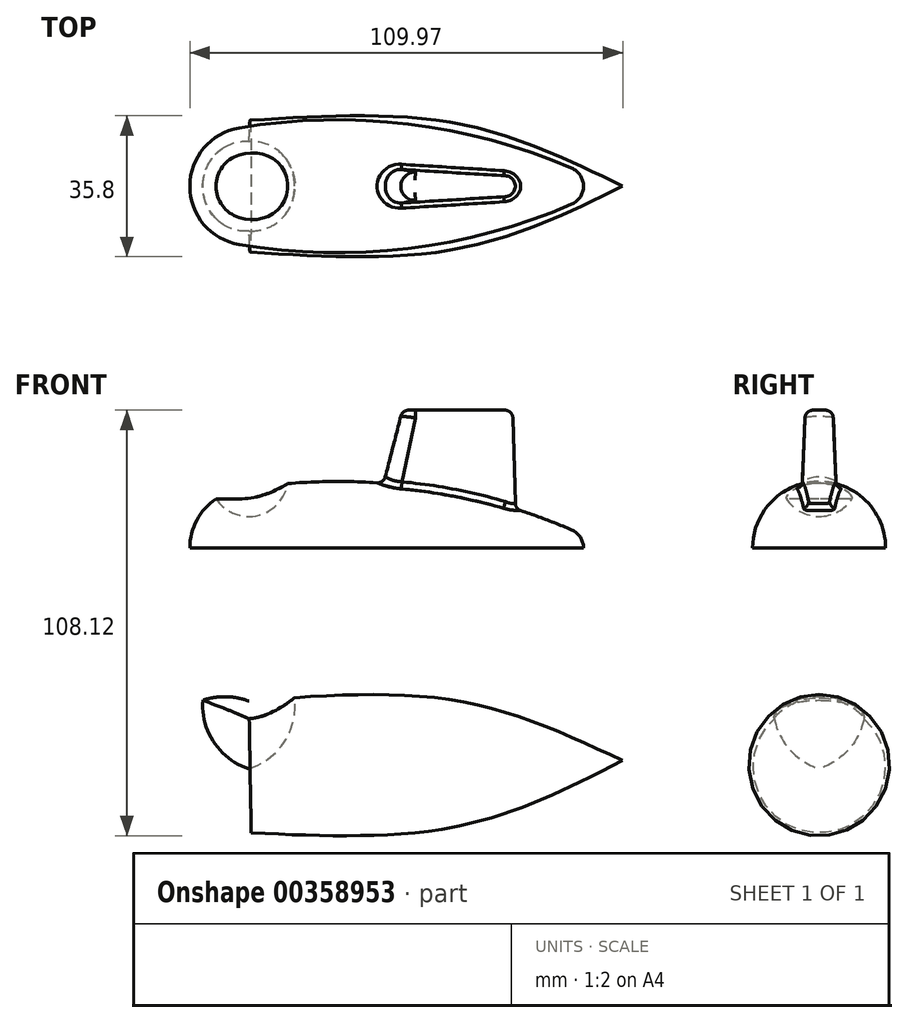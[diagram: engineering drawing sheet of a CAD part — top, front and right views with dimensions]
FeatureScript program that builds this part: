
annotation { "Feature Type Name" : "Feature", "Feature Type Description" : "" }
export const myFeature = defineFeature(function(context is Context, id is Id, definition is map)
    precondition{}
    {
        {
            var Q0;
            Q0=qCreatedBy(makeId("Top.planeOp"),FACE);
            var sketch = newSketch(context, id + "F0", { "sketchPlane" : qUnion([Q0])});
            skArc(sketch, "E0", {"start": v(-2.5, 14.8) * mm, "mid": v(-11.46, 9.68) * mm, "end": v(-15, 0) * mm});
            skArc(sketch, "E1", {"start": v(85, 0) * mm, "mid": v(84.18, 2.75) * mm, "end": v(81.98, 4.6) * mm});
            skArc(sketch, "E2", {"start": v(81.98, 4.6) * mm, "mid": v(40.48, 15.8) * mm, "end": v(-2.5, 14.8) * mm});
            skLineSegment(sketch, "E3", {"start": v(-15, 0) * mm, "end": v(85, 0) * mm});
            skSolve(sketch);
        }
        {
            var Q0;
            Q0=makeQuery(id+"F0.imprint","IMPRINT",FACE,{"disambiguationData":[TD([[makeQuery(id+"F0.imprint","IMPRINT",EDGE,{"derivedFrom":sQuery(id+"F0.wireOp",EDGE,"E0")}),1.0]])]});
            var Q1;
            Q1=sQuery(id+"F0.wireOp",EDGE,"E1");
            var Q2;
            Q2=sQuery(id+"F0.wireOp",EDGE,"E2");
            var Q3;
            Q3=sQuery(id+"F0.wireOp",EDGE,"E0");
            var Q4;
            Q4=sQuery(id+"F0.wireOp",EDGE,"E3");
            revolve(context, id + "F1", {"entities" : qUnion([Q0]), "surfaceEntities" : qUnion([Q1, Q2, Q3]), "axis" : qUnion([Q4]), "revolveType" : RevolveType.ONE_DIRECTION, "angle" : 180 * degree});
        }
        {
            var Q0;
            Q0=qCreatedBy(makeId("Front.planeOp"),FACE);
            var sketch = newSketch(context, id + "F2", { "sketchPlane" : qUnion([Q0])});
            skArc(sketch, "E4", {"start": v(0, 8) * mm, "mid": v(10, 18) * mm, "end": v(0, 28) * mm});
            skLineSegment(sketch, "E5", {"start": v(0, 28) * mm, "end": v(0, 8) * mm});
            skPoint(sketch, "E6.orphan", {"position": v(0, 42.91) * mm});
            skSolve(sketch);
        }
        {
            var Q0;
            Q0 = qSketchRegion(id + "F2", true);
            var Q1;
            Q1=sQuery(id+"F2.wireOp",EDGE,"E5");
            revolve(context, id + "F3", {"operationType" : NewBodyOperationType.REMOVE, "entities" : qUnion([Q0]), "axis" : qUnion([Q1]), "revolveType" : RevolveType.FULL, "oppositeDirection" : true});
        }
        {
            var Q0;
            Q0=qCreatedBy(makeId("Top.planeOp"),FACE);
            var sketch = newSketch(context, id + "F4", { "sketchPlane" : qUnion([Q0])});
            skArc(sketch, "E7", {"start": v(65.2, -3) * mm, "mid": v(68, 0) * mm, "end": v(65.2, 3) * mm});
            skArc(sketch, "E8", {"start": v(35.33, 4.99) * mm, "mid": v(30, 0) * mm, "end": v(35.33, -4.99) * mm});
            skLineSegment(sketch, "E9", {"start": v(35.33, -4.99) * mm, "end": v(65.2, -3) * mm});
            skLineSegment(sketch, "E10.MirrorCS", {"start": v(35.33, 4.99) * mm, "end": v(65.2, 3) * mm});
            skSolve(sketch);
        }
        {
            var Q0;
            Q0=qCreatedBy(makeId("Top.planeOp"),FACE);
            cPlane(context, id + "F5", {"entities" : qUnion([Q0]), "cplaneType" : CPlaneType.OFFSET, "offset" : 35 * mm, "width" : 150 * mm, "height" : 150 * mm});
        }
        {
            var Q0;
            Q0=qCreatedBy(id+"F5.planeOp",FACE);
            var sketch = newSketch(context, id + "F6", { "sketchPlane" : qUnion([Q0])});
            skArc(sketch, "E11", {"start": v(42.73, 3.5) * mm, "mid": v(39, 0) * mm, "end": v(42.73, -3.5) * mm});
            skArc(sketch, "E12", {"start": v(65.13, -2) * mm, "mid": v(67, 0) * mm, "end": v(65.13, 2) * mm});
            skLineSegment(sketch, "E13", {"start": v(65.13, -2) * mm, "end": v(42.73, -3.5) * mm});
            skLineSegment(sketch, "E14.MirrorCS", {"start": v(65.13, 2) * mm, "end": v(42.73, 3.5) * mm});
            skSolve(sketch);
        }
        {
            var Q1;
            Q1=makeQuery(id+"F4.imprint","IMPRINT",FACE,{"disambiguationData":[TD([[makeQuery(id+"F4.imprint","IMPRINT",EDGE,{"derivedFrom":sQuery(id+"F4.wireOp",EDGE,"E7")}),1.0]])]});
            var Q2;
            Q2=makeQuery(id+"F6.imprint","IMPRINT",FACE,{"disambiguationData":[TD([[makeQuery(id+"F6.imprint","IMPRINT",EDGE,{"derivedFrom":sQuery(id+"F6.wireOp",EDGE,"E11")}),1.0]])]});
            loft(context, id + "F7", {"operationType" : NewBodyOperationType.ADD, "sheetProfilesArray" : [{ "sheetProfileEntities" : qUnion([Q1]) }, { "sheetProfileEntities" : qUnion([Q2]) }]});
        }
        {
            var Q0;
            Q0=makeQuery(id+"F7.opLoft","CAP_FACE",FACE,{"disambiguationData":[OSD([makeQuery(id+"F6.imprint","IMPRINT",FACE,{"disambiguationData":[TD([[makeQuery(id+"F6.imprint","IMPRINT",EDGE,{"derivedFrom":sQuery(id+"F6.wireOp",EDGE,"E11")}),1.0]])]})])],"isStart":true});
            fillet(context, id + "F8", {"entities" : qUnion([Q0]), "radius" : 2 * mm, "tangentPropagation" : true, "allowEdgeOverflow" : false});
        }
        {
            var Q0;
            Q0=makeQuery(id+"F7.boolean.opBoolean","INTERSECT",EDGE,{"derivedFrom":[makeQuery(id+"F1.opRevolve","SWEPT_FACE",FACE,{"disambiguationData":[OSD([sQuery(id+"F0.wireOp",EDGE,"E2")])]}),makeQuery(id+"F7.opLoft","SWEPT_FACE",FACE,{"disambiguationData":[OSD([sQuery(id+"F4.wireOp",EDGE,"E7"),sQuery(id+"F4.wireOp",EDGE,"E8"),sQuery(id+"F4.wireOp",EDGE,"E9"),sQuery(id+"F6.wireOp",EDGE,"E11"),sQuery(id+"F6.wireOp",EDGE,"E12"),sQuery(id+"F6.wireOp",EDGE,"E13")])]})]});
            fillet(context, id + "F9", {"entities" : qUnion([Q0]), "radius" : 2 * mm, "tangentPropagation" : true, "allowEdgeOverflow" : false});
        }
        {
            var Q0;
            Q0=qCreatedBy(makeId("Front.planeOp"),FACE);
            var sketch = newSketch(context, id + "F10", { "sketchPlane" : qUnion([Q0])});
            skLineSegment(sketch, "E15", {"start": v(-23.84, -56.09) * mm, "end": v(94.97, -54.03) * mm});
            skArc(sketch, "E16", {"start": v(0, -38.92) * mm, "mid": v(-16.5, -41.13) * mm, "end": v(-23.84, -56.09) * mm});
            skFitSpline(sketch, "E17", {"points": [v(0, -38.92) * mm, v(53.3, -38.92) * mm, v(94.97, -54.03) * mm], "startDerivative": vector(105.71, 8.28) * mm, "endDerivative": vector(83.89, -39.23) * mm});
            skSolve(sketch);
        }
        {
            var Q0;
            Q0=makeQuery(id+"F10.imprint","IMPRINT",FACE,{"disambiguationData":[TD([[makeQuery(id+"F10.imprint","IMPRINT",EDGE,{"derivedFrom":sQuery(id+"F10.wireOp",EDGE,"E15")}),1.0]])]});
            var Q1;
            Q1=sQuery(id+"F10.wireOp",EDGE,"E15");
            revolve(context, id + "F11", {"entities" : qUnion([Q0]), "axis" : qUnion([Q1]), "revolveType" : RevolveType.FULL});
        }
        {
            var Q0;
            Q0=qCreatedBy(makeId("Front.planeOp"),FACE);
            var sketch = newSketch(context, id + "F12", { "sketchPlane" : qUnion([Q0])});
            skLineSegment(sketch, "E18", {"start": v(0, -24.04) * mm, "end": v(0, -56.09) * mm});
            skArc(sketch, "E19", {"start": v(0, -56.09) * mm, "mid": v(11.73, -40.06) * mm, "end": v(0, -24.04) * mm});
            skSolve(sketch);
        }
        {
            var Q0;
            Q0=makeQuery(id+"F12.imprint","IMPRINT",FACE,{"disambiguationData":[TD([[makeQuery(id+"F12.imprint","IMPRINT",EDGE,{"derivedFrom":sQuery(id+"F12.wireOp",EDGE,"E18")}),1.0]])]});
            var Q1;
            Q1=sQuery(id+"F12.wireOp",EDGE,"E18");
            revolve(context, id + "F13", {"operationType" : NewBodyOperationType.REMOVE, "entities" : qUnion([Q0]), "axis" : qUnion([Q1]), "revolveType" : RevolveType.FULL, "oppositeDirection" : true});
        }
        {
            var Q0;
            Q0=qCreatedBy(makeId("Top.planeOp"),FACE);
            cPlane(context, id + "F14", {"entities" : qUnion([Q0]), "cplaneType" : CPlaneType.OFFSET, "offset" : 63 * mm, "oppositeDirection" : true, "width" : 150 * mm, "height" : 150 * mm});
        }
    });
